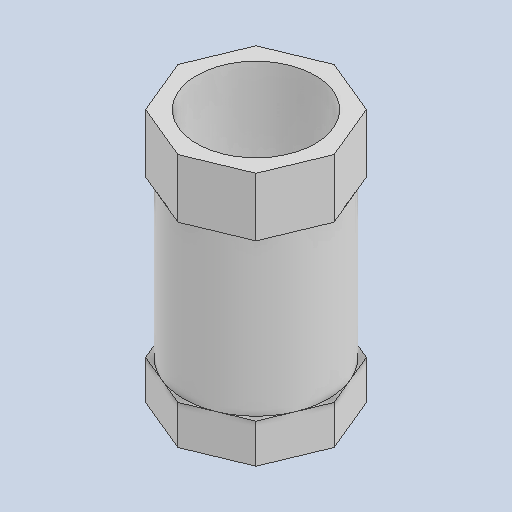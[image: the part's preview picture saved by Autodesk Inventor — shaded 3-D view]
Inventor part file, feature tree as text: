
AUTODESK INVENTOR PART (.ipt)
format: ipt  version: 2024 (Build 280153000, 153)  size: 145,920 bytes
history: native  units: mm
features: other x4, sketch x4
ambient origin geometry x8: Origin, YZ Plane, XZ Plane, XY Plane, X Axis, Y Axis, Z Axis, Center Point
bodies: Body1 (feature_tree)
feature tree (8):
  other  "TUBO_METALICO_B.ipt"
  other  "Sólido1::TUBO_METALICO_B.ipt"
  other  "OperaciónIdentificador1"
  sketch  "Boceto1"  dims[d0=10.0mm]
  sketch  "Boceto2"
  sketch  "Boceto3"
  sketch  "Boceto4"
  other  "Sólido1"
